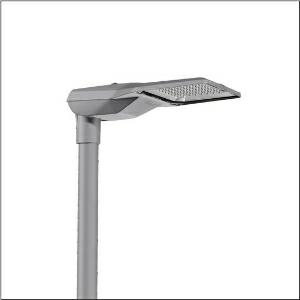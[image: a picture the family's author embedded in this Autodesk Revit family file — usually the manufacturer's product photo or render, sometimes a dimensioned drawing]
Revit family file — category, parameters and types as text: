
# Revit family: streetlight_sl_21_iq_midi___p0_8a_5xe3u31v08nb_7897
name_source: partatom
category: Lighting Fixtures
units: mm (PartAtom-declared; Revit-internal decimal feet)

## family parameters
Cut with Voids When Loaded = No
Host = Face
Light Source = No
Part Type = Normal
Room Calculation Point = No
Round Connector Dimension = Use Diameter
Shared = No

## types (1)
- --- (1 x LED, 21740 lm, 136.6 W, 3000K)
    Apparent Load = 137 VA
    CIE Flux Codes = 36 69 97 100 100
    Color Rendering = 70
    Color Temperature = 3000K
    Default Elevation = 1800 mm
    Description = Streetlight SL 21 iQ midi, mast luminaire, primary light control with lens, of PMMA, primary optical cover: cover, of toughened safety glass, transparent, light distribution: P0.8a, light emission: direct distribution, primary light characteristic: asymmetric, installation type: post-top, side-entry, LED, High Power LED, rated luminous flux: 21.740lm, luminous efficacy: 159lm/W, light colour: 730, colour temperature: 3000K, control gear: iQ-Street Remote, D4i with power reduction, control: pre-setting: logarithmic dimming characteristic, Street-Remote, Auto-Match, Temp-Guard, Lumen-Switch, Night-Set, Smart-Wire, Light-Fading, Desk-Remote (wireless, voltage-free reading and setting of iQ features in the workshop via application-optimized NFC function/RFID function), optimised constant luminous flux control (CLO 2.0), mains connection: 230..240V, AC, 50/60Hz, start of lifetime: 137W, end of service life: 144W, reduction: 61W, luminaire housing, of diecast aluminium, powder-coated, SITECO metallic grey (DB 702S), corrosivity category C5 high according to DIN EN ISO 12944, please order mast flange separately, inclination adjustable: 0°, 5°, 10°, 15°, sealing non-destructively replaceable, multi-level sealing system, length: 644mm, width: 335mm, height: 110mm, mast flange for spigot size: 42mm (side-entry): 5XC10008XM4, 60/48mm (side-entry/post-top): 5XC10108XM2, 76/60mm (side-entry/post-top): 5XC10108XM1, mounting height: 4..8m, Smart Interface above, protection rating (complete): IP66, insulation class (complete): insulation class II (safety insulation), certification: CE, ENEC, ENEC+, VDE, impact resistance: IK10, permissible operating ambient temperature for outdoor applications: -40..+50°C, standard-compliant lighting for roads and squares, packaging unit: 1 piece

Light Distribution: P0.8a
    Height = 111 mm
    Lamp = 1 x LED
    Lamp Light Flux = 21740 lm
    Lamp Power = 136.6 W
    Lamp count = 1
    Length = 644 mm
    Luminous efficacy = 159 lm/W
    Manufacturer = Siteco
    ModVariant = No
    Model = 5XE3U31V08NB
    Number of Poles = 1
    OnlyDefault = Yes
    Power Factor = 1
    Product Name = Streetlight SL 21 iQ midi | P0.8a
    Product group = mast luminaire | pylon top
    ProductGroupID = 6100
    Protection Class = Protection class II
    Protection Degree = IP 66
    RLX_Detail_Level = 1
    RLX_Emergency_Light_Flux = 0 lm
    RLX_Emergency_Type = 0
    RLX_Emergency_Type_DB = No
    RlxData = <blob elided: 90857 chars, md5=18caea22>
    Socket = socket
    Standby Power = 0 W
    System Light Flux = 21740 lm
    System Power = 137 W
    Type Comments = factory setting: luminous flux: 100 % | dim-lin: 254 | 733 mA
    Type Image = l_1004302.jpg
    URL = http://relux.com
    VarID = @adj_079763
    Voltage = 0 V
    Weight = 0.00 kg
    Width = 336 mm

## geometry (parser evidence)
native form markers: Blend x4, Sweep x10
no freeform markers — native parametric forms only
